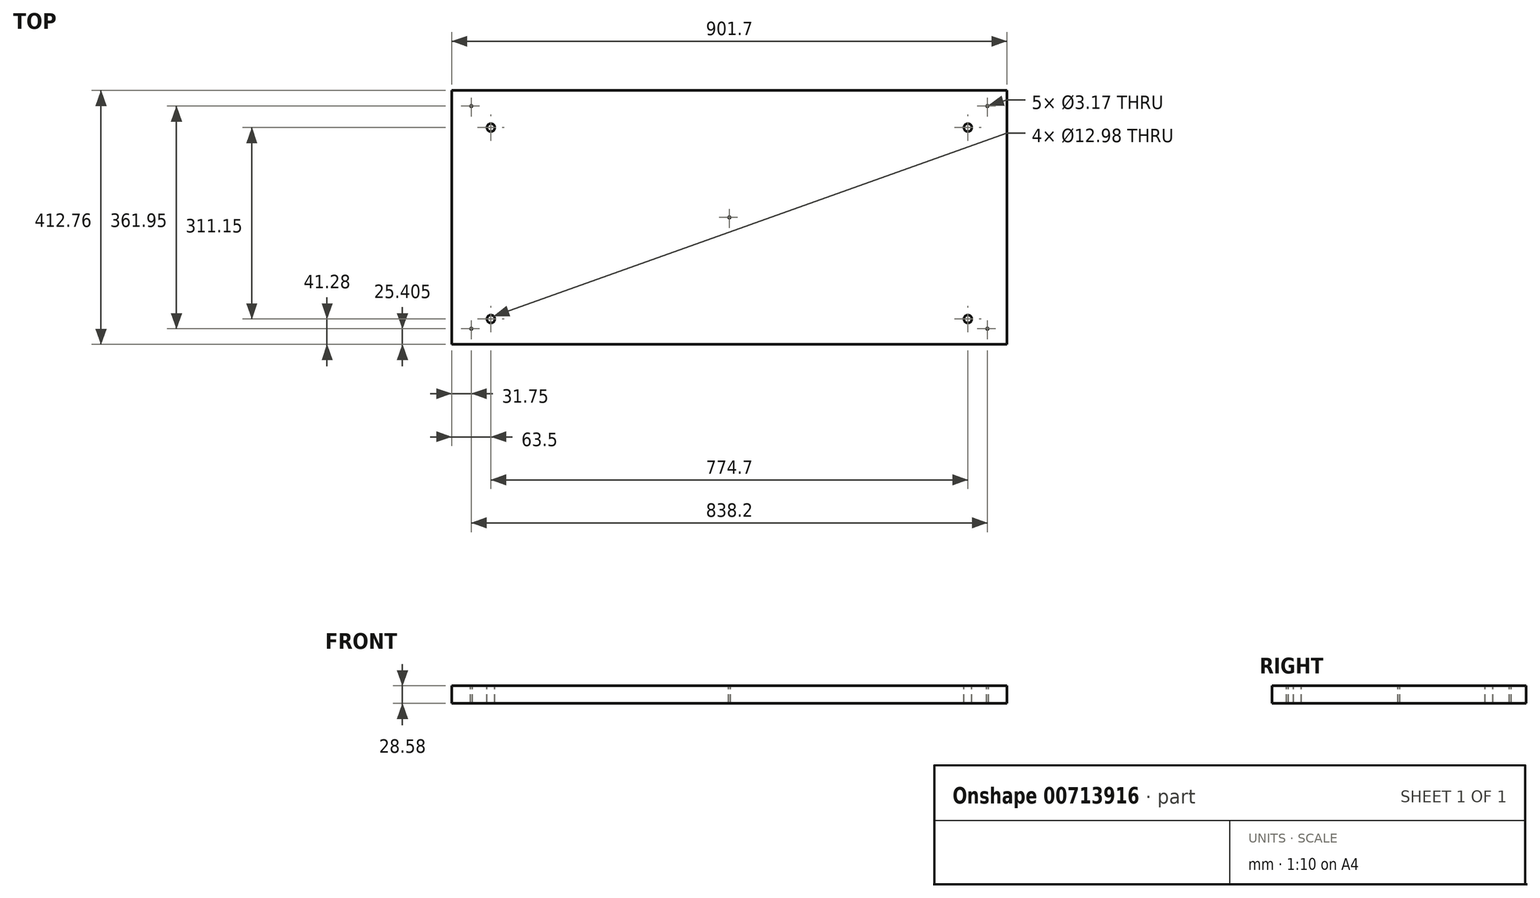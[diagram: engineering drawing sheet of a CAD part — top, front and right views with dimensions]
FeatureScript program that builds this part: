
annotation { "Feature Type Name" : "Feature", "Feature Type Description" : "" }
export const myFeature = defineFeature(function(context is Context, id is Id, definition is map)
    precondition{}
    {
        {
            var Q0;
            Q0=qCreatedBy(makeId("Top.planeOp"),FACE);
            var sketch = newSketch(context, id + "F0", { "sketchPlane" : qUnion([Q0])});
            skLineSegment(sketch, "E0.bottom", {"start": v(-450.85, 206.37) * mm, "end": v(450.85, 206.37) * mm});
            skLineSegment(sketch, "E0.top", {"start": v(-450.85, -206.38) * mm, "end": v(450.85, -206.38) * mm});
            skLineSegment(sketch, "E0.left", {"start": v(-450.85, 206.37) * mm, "end": v(-450.85, -206.38) * mm});
            skLineSegment(sketch, "E0.right", {"start": v(450.85, 206.37) * mm, "end": v(450.85, -206.38) * mm});
            skPoint(sketch, "E0.middle", {"position": v(0, 0) * mm});
            skSolve(sketch);
        }
        {
            var Q0;
            Q0=makeQuery(id+"F0.imprint","IMPRINT",FACE,{"disambiguationData":[TD([[makeQuery(id+"F0.imprint","IMPRINT",EDGE,{"derivedFrom":sQuery(id+"F0.wireOp",EDGE,"E0.bottom")}),-1.0]])]});
            extrude(context, id + "F1", {"entities" : qUnion([Q0]), "depth" : 28.57 * mm, "offsetDistance" : 25.4 * mm});
        }
        {
            var Q0;
            Q0=makeQuery(id+"F1.opExtrude","CAP_FACE",FACE,{"disambiguationData":[OSD([sQuery(id+"F0.wireOp",EDGE,"E0.bottom"),sQuery(id+"F0.wireOp",EDGE,"E0.top"),sQuery(id+"F0.wireOp",EDGE,"E0.left"),sQuery(id+"F0.wireOp",EDGE,"E0.right")])],"isStart":false});
            var sketch = newSketch(context, id + "F2", { "sketchPlane" : qUnion([Q0])});
            skLineSegment(sketch, "E1", {"start": v(0, 0) * mm, "end": v(0, -9.52) * mm});
            skLineSegment(sketch, "E2.bottom", {"start": v(387.35, 146.05) * mm, "end": v(-387.35, 146.05) * mm});
            skLineSegment(sketch, "E2.top", {"start": v(387.35, -165.1) * mm, "end": v(-387.35, -165.1) * mm});
            skLineSegment(sketch, "E2.left", {"start": v(387.35, 146.05) * mm, "end": v(387.35, -165.1) * mm});
            skLineSegment(sketch, "E2.right", {"start": v(-387.35, 146.05) * mm, "end": v(-387.35, -165.1) * mm});
            skPoint(sketch, "E2.middle", {"position": v(0, -9.52) * mm});
            skSolve(sketch);
        }
        {
            var Q0;
            Q0=sQuery(id+"F2.wireOp",VERTEX,"E2.bottom.end");
            var Q1;
            Q1=sQuery(id+"F2.wireOp",VERTEX,"E2.top.end");
            var Q2;
            Q2=sQuery(id+"F2.wireOp",VERTEX,"E2.top.start");
            var Q3;
            Q3=sQuery(id+"F2.wireOp",VERTEX,"E2.left.start");
            var Q4;
            Q4=makeQuery(id+"F1.opExtrude","SWEPT_BODY",BODY,{"disambiguationData":[OSD([sQuery(id+"F0.wireOp",EDGE,"E0.bottom"),sQuery(id+"F0.wireOp",EDGE,"E0.top"),sQuery(id+"F0.wireOp",EDGE,"E0.left"),sQuery(id+"F0.wireOp",EDGE,"E0.right")])]});
            hole(context, id + "F3", {"style" : HoleStyle.SIMPLE, "endStyle" : HoleEndStyle.BLIND, "holeDiameter" : 12.98 * mm, "majorDiameter" : 6.35 * mm, "holeDepth" : 31.75 * mm, "isTappedThrough" : true, "tappedDepth" : 12.7 * mm, "tapClearance" : 3, "startFromSketch" : true, "locations" : qUnion([Q0, Q1, Q2, Q3]), "scope" : qUnion([Q4])});
        }
        {
            var Q0;
            Q0=makeQuery(id+"F1.opExtrude","CAP_FACE",FACE,{"disambiguationData":[OSD([sQuery(id+"F0.wireOp",EDGE,"E0.bottom"),sQuery(id+"F0.wireOp",EDGE,"E0.top"),sQuery(id+"F0.wireOp",EDGE,"E0.left"),sQuery(id+"F0.wireOp",EDGE,"E0.right")])],"isStart":false});
            var sketch = newSketch(context, id + "F4", { "sketchPlane" : qUnion([Q0])});
            skLineSegment(sketch, "E3.bottom", {"start": v(419.1, 180.98) * mm, "end": v(-419.1, 180.98) * mm});
            skLineSegment(sketch, "E3.top", {"start": v(419.1, -180.98) * mm, "end": v(-419.1, -180.98) * mm});
            skLineSegment(sketch, "E3.left", {"start": v(419.1, 180.98) * mm, "end": v(419.1, -180.98) * mm});
            skLineSegment(sketch, "E3.right", {"start": v(-419.1, 180.98) * mm, "end": v(-419.1, -180.98) * mm});
            skPoint(sketch, "E3.middle", {"position": v(0, 0) * mm});
            skSolve(sketch);
        }
        {
            var Q0;
            Q0=sQuery(id+"F4.wireOp",VERTEX,"E3.right.start");
            var Q1;
            Q1=sQuery(id+"F4.wireOp",VERTEX,"E3.right.end");
            var Q2;
            Q2=sQuery(id+"F4.wireOp",VERTEX,"E3.left.end");
            var Q3;
            Q3=sQuery(id+"F4.wireOp",VERTEX,"E3.bottom.start");
            var Q4;
            Q4=sQuery(id+"F4.wireOp",VERTEX,"E3.middle");
            var Q5;
            Q5=makeQuery(id+"F1.opExtrude","SWEPT_BODY",BODY,{"disambiguationData":[OSD([sQuery(id+"F0.wireOp",EDGE,"E0.bottom"),sQuery(id+"F0.wireOp",EDGE,"E0.top"),sQuery(id+"F0.wireOp",EDGE,"E0.left"),sQuery(id+"F0.wireOp",EDGE,"E0.right")])]});
            hole(context, id + "F5", {"style" : HoleStyle.SIMPLE, "endStyle" : HoleEndStyle.BLIND, "holeDiameter" : 3.17 * mm, "majorDiameter" : 6.35 * mm, "holeDepth" : 31.75 * mm, "isTappedThrough" : true, "tappedDepth" : 12.7 * mm, "tapClearance" : 3, "startFromSketch" : true, "locations" : qUnion([Q0, Q1, Q2, Q3, Q4]), "scope" : qUnion([Q5])});
        }
    });
